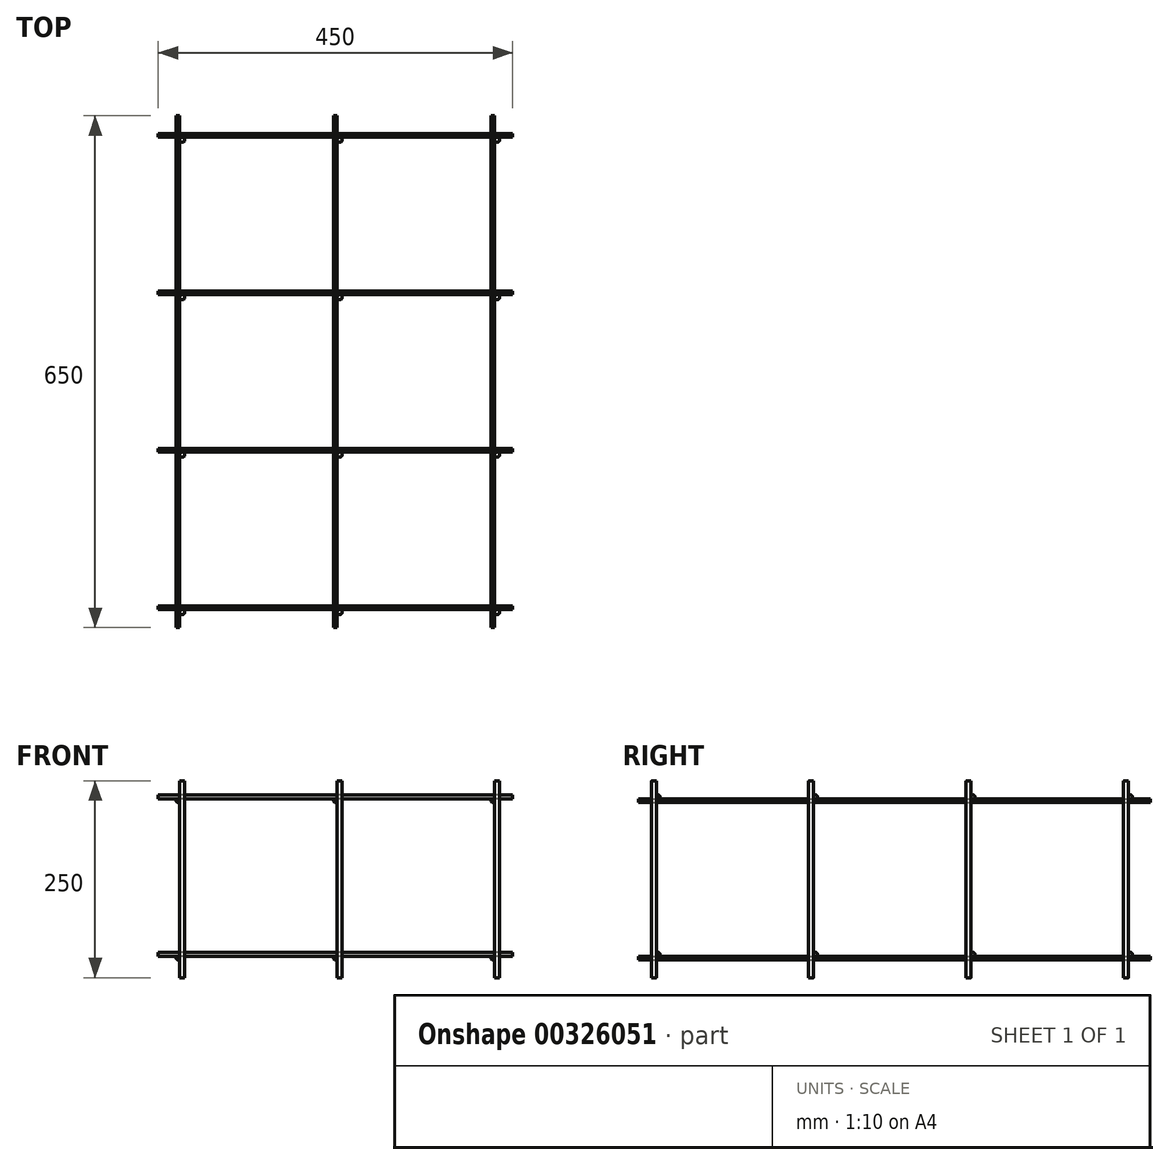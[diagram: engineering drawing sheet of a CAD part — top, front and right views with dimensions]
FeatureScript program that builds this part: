
annotation { "Feature Type Name" : "Feature", "Feature Type Description" : "" }
export const myFeature = defineFeature(function(context is Context, id is Id, definition is map)
    precondition{}
    {
        {
            var Q0;
            Q0=qCreatedBy(makeId("Front.planeOp"),FACE);
            var sketch = newSketch(context, id + "F0", { "sketchPlane" : qUnion([Q0])});
            skLineSegment(sketch, "E0.bottom", {"start": v(-200, 100) * mm, "end": v(0, 100) * mm, "construction": true});
            skLineSegment(sketch, "E0.top", {"start": v(-200, -100) * mm, "end": v(0, -100) * mm, "construction": true});
            skLineSegment(sketch, "E0.left", {"start": v(-200, 100) * mm, "end": v(-200, -100) * mm, "construction": true});
            skLineSegment(sketch, "E0.right", {"start": v(0, 100) * mm, "end": v(0, -100) * mm, "construction": true});
            skLineSegment(sketch, "E1.bottom", {"start": v(0, 100) * mm, "end": v(200, 100) * mm, "construction": true});
            skLineSegment(sketch, "E1.top", {"start": v(0, -100) * mm, "end": v(200, -100) * mm, "construction": true});
            skLineSegment(sketch, "E1.right", {"start": v(200, 100) * mm, "end": v(200, -100) * mm, "construction": true});
            skLineSegment(sketch, "E2.bottom", {"start": v(-250, 150) * mm, "end": v(250, 150) * mm, "construction": true});
            skLineSegment(sketch, "E2.top", {"start": v(-250, -150) * mm, "end": v(250, -150) * mm, "construction": true});
            skLineSegment(sketch, "E2.left", {"start": v(-250, 150) * mm, "end": v(-250, -150) * mm, "construction": true});
            skLineSegment(sketch, "E2.right", {"start": v(250, 150) * mm, "end": v(250, -150) * mm, "construction": true});
            skPoint(sketch, "E2.middle", {"position": v(0, 0) * mm});
            skCircle(sketch, "E3", {"center": v(-200, 100) * mm, "radius": 2.38 * mm});
            skCircle(sketch, "E4", {"center": v(0, 100) * mm, "radius": 2.38 * mm});
            skCircle(sketch, "E5", {"center": v(200, 100) * mm, "radius": 2.38 * mm});
            skCircle(sketch, "E6", {"center": v(200, -100) * mm, "radius": 2.38 * mm});
            skCircle(sketch, "E7", {"center": v(0, -100) * mm, "radius": 2.38 * mm});
            skCircle(sketch, "E8", {"center": v(-200, -100) * mm, "radius": 2.38 * mm});
            skSolve(sketch);
        }
        {
            var Q0;
            Q0 = qSketchRegion(id + "F0", true);
            extrude(context, id + "F1", {"entities" : qUnion([Q0]), "endBound" : BoundingType.SYMMETRIC, "depth" : 650 * mm});
        }
        {
            var Q0;
            Q0=qCreatedBy(makeId("Right.planeOp"),FACE);
            var sketch = newSketch(context, id + "F2", { "sketchPlane" : qUnion([Q0])});
            skLineSegment(sketch, "E9.bottom", {"start": v(100, 104.76) * mm, "end": v(-100, 104.76) * mm, "construction": true});
            skLineSegment(sketch, "E9.top", {"start": v(100, -95.24) * mm, "end": v(-100, -95.24) * mm, "construction": true});
            skLineSegment(sketch, "E9.left", {"start": v(100, 104.76) * mm, "end": v(100, -95.24) * mm, "construction": true});
            skLineSegment(sketch, "E9.right", {"start": v(-100, 104.76) * mm, "end": v(-100, -95.24) * mm, "construction": true});
            skLineSegment(sketch, "E10.bottom", {"start": v(-100, 104.76) * mm, "end": v(-300, 104.76) * mm, "construction": true});
            skLineSegment(sketch, "E10.top", {"start": v(-100, -95.24) * mm, "end": v(-300, -95.24) * mm, "construction": true});
            skLineSegment(sketch, "E10.right", {"start": v(-300, 104.76) * mm, "end": v(-300, -95.24) * mm, "construction": true});
            skLineSegment(sketch, "E11.bottom", {"start": v(100, -95.24) * mm, "end": v(300, -95.24) * mm, "construction": true});
            skLineSegment(sketch, "E11.top", {"start": v(100, 104.76) * mm, "end": v(300, 104.76) * mm, "construction": true});
            skLineSegment(sketch, "E11.left", {"start": v(100, -95.24) * mm, "end": v(100, 104.76) * mm, "construction": true});
            skLineSegment(sketch, "E11.right", {"start": v(300, -95.24) * mm, "end": v(300, 104.76) * mm, "construction": true});
            skLineSegment(sketch, "E12.bottom", {"start": v(-400, 150) * mm, "end": v(400, 150) * mm, "construction": true});
            skLineSegment(sketch, "E12.top", {"start": v(-400, -150) * mm, "end": v(400, -150) * mm, "construction": true});
            skLineSegment(sketch, "E12.left", {"start": v(-400, 150) * mm, "end": v(-400, -150) * mm, "construction": true});
            skLineSegment(sketch, "E12.right", {"start": v(400, 150) * mm, "end": v(400, -150) * mm, "construction": true});
            skCircle(sketch, "E13", {"center": v(-300, 104.76) * mm, "radius": 2.38 * mm});
            skCircle(sketch, "E14", {"center": v(-100, 104.76) * mm, "radius": 2.38 * mm});
            skCircle(sketch, "E15", {"center": v(100, 104.76) * mm, "radius": 2.38 * mm});
            skCircle(sketch, "E16", {"center": v(300, 104.76) * mm, "radius": 2.38 * mm});
            skCircle(sketch, "E17", {"center": v(300, -95.24) * mm, "radius": 2.38 * mm});
            skCircle(sketch, "E18", {"center": v(100, -95.24) * mm, "radius": 2.38 * mm});
            skCircle(sketch, "E19", {"center": v(-100, -95.24) * mm, "radius": 2.38 * mm});
            skCircle(sketch, "E20", {"center": v(-300, -95.24) * mm, "radius": 2.38 * mm});
            skLineSegment(sketch, "E21", {"start": v(-400, 150) * mm, "end": v(400, -150) * mm, "construction": true});
            skLineSegment(sketch, "E22", {"start": v(0, 104.76) * mm, "end": v(0, -95.24) * mm, "construction": true});
            skLineSegment(sketch, "E23", {"start": v(-325, 102.38) * mm, "end": v(325, 102.38) * mm, "construction": true});
            skSolve(sketch);
        }
        {
            var Q0;
            Q0 = qSketchRegion(id + "F2", true);
            extrude(context, id + "F3", {"entities" : qUnion([Q0]), "endBound" : BoundingType.SYMMETRIC, "depth" : 450 * mm});
        }
        {
            var Q0;
            Q0=qCreatedBy(makeId("Top.planeOp"),FACE);
            var sketch = newSketch(context, id + "F4", { "sketchPlane" : qUnion([Q0])});
            skLineSegment(sketch, "E24", {"start": v(-197.62, 325) * mm, "end": v(-197.62, -325) * mm, "construction": true});
            skLineSegment(sketch, "E25", {"start": v(225, 297.62) * mm, "end": v(-225, 297.62) * mm, "construction": true});
            skLineSegment(sketch, "E26", {"start": v(2.38, 325) * mm, "end": v(2.38, -325) * mm, "construction": true});
            skLineSegment(sketch, "E27", {"start": v(225, 97.62) * mm, "end": v(-225, 97.62) * mm, "construction": true});
            skLineSegment(sketch, "E28", {"start": v(205.56, -102.38) * mm, "end": v(-225, -102.38) * mm, "construction": true});
            skLineSegment(sketch, "E29", {"start": v(225, -302.38) * mm, "end": v(-225, -302.38) * mm, "construction": true});
            skLineSegment(sketch, "E30", {"start": v(202.38, 325) * mm, "end": v(202.38, -325) * mm, "construction": true});
            skCircle(sketch, "E31", {"center": v(-194.44, 294.44) * mm, "radius": 3.18 * mm});
            skCircle(sketch, "E32", {"center": v(5.56, 294.44) * mm, "radius": 3.18 * mm});
            skCircle(sketch, "E33", {"center": v(-194.44, 94.44) * mm, "radius": 3.18 * mm});
            skCircle(sketch, "E34", {"center": v(5.56, 94.44) * mm, "radius": 3.18 * mm});
            skCircle(sketch, "E35", {"center": v(-194.44, -105.56) * mm, "radius": 3.18 * mm});
            skCircle(sketch, "E36", {"center": v(5.56, -105.56) * mm, "radius": 3.18 * mm});
            skCircle(sketch, "E37", {"center": v(205.56, 294.44) * mm, "radius": 3.18 * mm});
            skCircle(sketch, "E38", {"center": v(205.56, 94.44) * mm, "radius": 3.18 * mm});
            skCircle(sketch, "E39", {"center": v(205.56, -105.56) * mm, "radius": 3.18 * mm});
            skCircle(sketch, "E40", {"center": v(-194.44, -305.56) * mm, "radius": 3.18 * mm});
            skCircle(sketch, "E41", {"center": v(5.56, -305.56) * mm, "radius": 3.18 * mm});
            skCircle(sketch, "E42", {"center": v(205.56, -305.56) * mm, "radius": 3.18 * mm});
            skSolve(sketch);
        }
        {
            var Q0;
            Q0 = qSketchRegion(id + "F4", true);
            extrude(context, id + "F5", {"entities" : qUnion([Q0]), "endBound" : BoundingType.SYMMETRIC, "depth" : 250 * mm});
        }
    });
